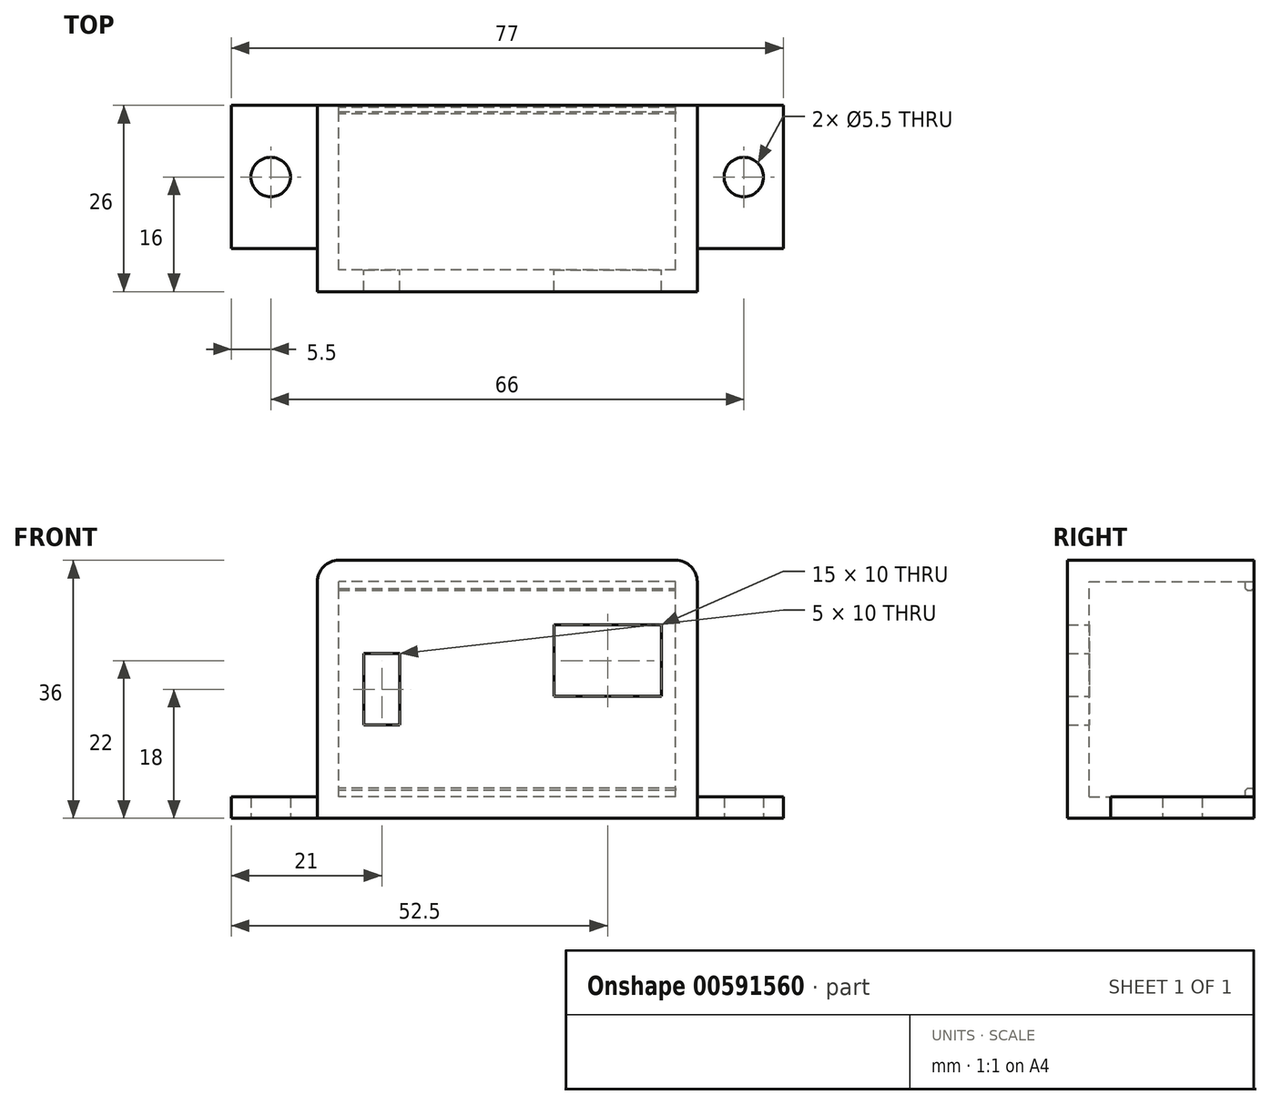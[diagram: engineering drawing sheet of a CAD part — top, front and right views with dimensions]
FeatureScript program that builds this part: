
annotation { "Feature Type Name" : "Feature", "Feature Type Description" : "" }
export const myFeature = defineFeature(function(context is Context, id is Id, definition is map)
    precondition{}
    {
        {
            var Q0;
            Q0=qCreatedBy(makeId("Front.planeOp"),FACE);
            var sketch = newSketch(context, id + "F0", { "sketchPlane" : qUnion([Q0])});
            skLineSegment(sketch, "E0.bottom", {"start": v(26.5, -18) * mm, "end": v(-26.5, -18) * mm});
            skLineSegment(sketch, "E0.top", {"start": v(26.5, 18) * mm, "end": v(-26.5, 18) * mm});
            skLineSegment(sketch, "E0.left", {"start": v(26.5, -18) * mm, "end": v(26.5, 18) * mm});
            skLineSegment(sketch, "E0.right", {"start": v(-26.5, -18) * mm, "end": v(-26.5, 18) * mm});
            skPoint(sketch, "E0.middle", {"position": v(0, 0) * mm});
            skLineSegment(sketch, "E1.bottom", {"start": v(23.5, -15) * mm, "end": v(-23.5, -15) * mm});
            skLineSegment(sketch, "E1.top", {"start": v(23.5, 15) * mm, "end": v(-23.5, 15) * mm});
            skLineSegment(sketch, "E1.left", {"start": v(23.5, -15) * mm, "end": v(23.5, 15) * mm});
            skLineSegment(sketch, "E1.right", {"start": v(-23.5, -15) * mm, "end": v(-23.5, 15) * mm});
            skLineSegment(sketch, "E2.bottom", {"start": v(26.5, -18) * mm, "end": v(38.5, -18) * mm});
            skLineSegment(sketch, "E2.top", {"start": v(26.5, -15) * mm, "end": v(38.5, -15) * mm});
            skLineSegment(sketch, "E2.left", {"start": v(26.5, -18) * mm, "end": v(26.5, -15) * mm});
            skLineSegment(sketch, "E2.right", {"start": v(38.5, -18) * mm, "end": v(38.5, -15) * mm});
            skLineSegment(sketch, "E3.bottom", {"start": v(-26.5, -18) * mm, "end": v(-38.5, -18) * mm});
            skLineSegment(sketch, "E3.top", {"start": v(-26.5, -15) * mm, "end": v(-38.5, -15) * mm});
            skLineSegment(sketch, "E3.left", {"start": v(-26.5, -18) * mm, "end": v(-26.5, -15) * mm});
            skLineSegment(sketch, "E3.right", {"start": v(-38.5, -18) * mm, "end": v(-38.5, -15) * mm});
            skSolve(sketch);
        }
        {
            var Q0;
            Q0=makeQuery(id+"F0.imprint","IMPRINT",FACE,{"disambiguationData":[TD([[makeQuery(id+"F0.imprint","IMPRINT",EDGE,{"derivedFrom":sQuery(id+"F0.wireOp",EDGE,"E0.bottom")}),-1.0]])]});
            extrude(context, id + "F1", {"entities" : qUnion([Q0]), "depth" : 23 * mm, "offsetDistance" : 25 * mm});
        }
        {
            var Q0;
            Q0=makeQuery(id+"F0.imprint","IMPRINT",FACE,{"disambiguationData":[TD([[makeQuery(id+"F0.imprint","IMPRINT",EDGE,{"derivedFrom":sQuery(id+"F0.wireOp",EDGE,"E3.bottom")}),-1.0]])]});
            var Q1;
            Q1=makeQuery(id+"F0.imprint","IMPRINT",FACE,{"disambiguationData":[TD([[makeQuery(id+"F0.imprint","IMPRINT",EDGE,{"derivedFrom":sQuery(id+"F0.wireOp",EDGE,"E2.bottom")}),1.0]])]});
            extrude(context, id + "F2", {"entities" : qUnion([Q0, Q1]), "operationType" : NewBodyOperationType.ADD, "depth" : 20 * mm, "offsetDistance" : 25 * mm});
        }
        {
            var Q0;
            Q0=makeQuery(id+"F1.opExtrude","CAP_FACE",FACE,{"disambiguationData":[OSD([sQuery(id+"F0.wireOp",EDGE,"E0.bottom"),sQuery(id+"F0.wireOp",EDGE,"E0.top"),sQuery(id+"F0.wireOp",EDGE,"E0.left"),sQuery(id+"F0.wireOp",EDGE,"E0.right"),sQuery(id+"F0.wireOp",EDGE,"E1.bottom"),sQuery(id+"F0.wireOp",EDGE,"E1.top"),sQuery(id+"F0.wireOp",EDGE,"E1.left"),sQuery(id+"F0.wireOp",EDGE,"E1.right"),sQuery(id+"F0.wireOp",EDGE,"E2.bottom"),sQuery(id+"F0.wireOp",EDGE,"E2.top"),sQuery(id+"F0.wireOp",EDGE,"E2.right"),sQuery(id+"F0.wireOp",EDGE,"E3.bottom"),sQuery(id+"F0.wireOp",EDGE,"E3.top"),sQuery(id+"F0.wireOp",EDGE,"E3.right")])],"isStart":true});
            var sketch = newSketch(context, id + "F3", { "sketchPlane" : qUnion([Q0])});
            skLineSegment(sketch, "E4.bottom", {"start": v(23.5, -13.8) * mm, "end": v(-23.5, -13.8) * mm});
            skLineSegment(sketch, "E4.top", {"start": v(23.5, 13.8) * mm, "end": v(-23.5, 13.8) * mm});
            skLineSegment(sketch, "E4.left", {"start": v(23.5, -13.8) * mm, "end": v(23.5, 13.8) * mm});
            skLineSegment(sketch, "E4.right", {"start": v(-23.5, -13.8) * mm, "end": v(-23.5, 13.8) * mm});
            skPoint(sketch, "E4.middle", {"position": v(0, 0) * mm});
            skSolve(sketch);
        }
        {
            var Q0;
            {var subQ0=sQuery(id+"F3.wireOp",EDGE,"E4.top");Q0=makeQuery(id+"F3.imprint","IMPRINT",FACE,{"disambiguationData":[TD([[makeQuery(id+"F3.imprint","IMPRINT",EDGE,{"derivedFrom":subQ0}),-1.0]])]});}
            var Q1;
            {var subQ0=sQuery(id+"F3.wireOp",EDGE,"E4.bottom");Q1=makeQuery(id+"F3.imprint","IMPRINT",FACE,{"disambiguationData":[TD([[makeQuery(id+"F3.imprint","IMPRINT",EDGE,{"derivedFrom":subQ0}),1.0]])]});}
            extrude(context, id + "F4", {"entities" : qUnion([Q0, Q1]), "oppositeDirection" : true, "depth" : 1.2 * mm, "offsetDistance" : 25 * mm});
        }
        {
            var Q0;
            Q0=makeQuery(id+"F4.opExtrude","CAP_EDGE",EDGE,{"disambiguationData":[OSD([sQuery(id+"F3.wireOp",EDGE,"E4.bottom")])],"isStart":true});
            var Q1;
            Q1=makeQuery(id+"F4.opExtrude","CAP_EDGE",EDGE,{"disambiguationData":[OSD([sQuery(id+"F3.wireOp",EDGE,"E4.bottom")])],"isStart":false});
            var Q2;
            Q2=makeQuery(id+"F4.opExtrude","CAP_EDGE",EDGE,{"disambiguationData":[OSD([sQuery(id+"F3.wireOp",EDGE,"E4.top")])],"isStart":true});
            var Q3;
            Q3=makeQuery(id+"F4.opExtrude","CAP_EDGE",EDGE,{"disambiguationData":[OSD([sQuery(id+"F3.wireOp",EDGE,"E4.top")])],"isStart":false});
            chamfer(context, id + "F5", {"entities" : qUnion([Q0, Q1, Q2, Q3]), "width" : .3 * mm, "tangentPropagation" : true});
        }
        {
            var Q0;
            Q0=makeQuery(id+"F2.opExtrude","SWEPT_FACE",FACE,{"disambiguationData":[OSD([sQuery(id+"F0.wireOp",EDGE,"E3.top")])]});
            var sketch = newSketch(context, id + "F6", { "sketchPlane" : qUnion([Q0])});
            skPoint(sketch, "E5", {"position": v(-33, -10) * mm});
            skSolve(sketch);
        }
        {
            var Q0;
            Q0=makeQuery(id+"F2.opExtrude","SWEPT_FACE",FACE,{"disambiguationData":[OSD([sQuery(id+"F0.wireOp",EDGE,"E2.top")])]});
            var sketch = newSketch(context, id + "F7", { "sketchPlane" : qUnion([Q0])});
            skPoint(sketch, "E6", {"position": v(33, -10) * mm});
            skSolve(sketch);
        }
        {
            var Q0;
            Q0=sQuery(id+"F6.wireOp",VERTEX,"E5");
            var Q1;
            Q1=sQuery(id+"F7.wireOp",VERTEX,"E6");
            var Q2;
            Q2=makeQuery(id+"F1.opExtrude","SWEPT_BODY",BODY,{"disambiguationData":[OSD([sQuery(id+"F0.wireOp",EDGE,"E0.bottom"),sQuery(id+"F0.wireOp",EDGE,"E0.top"),sQuery(id+"F0.wireOp",EDGE,"E0.left"),sQuery(id+"F0.wireOp",EDGE,"E0.right"),sQuery(id+"F0.wireOp",EDGE,"E1.bottom"),sQuery(id+"F0.wireOp",EDGE,"E1.top"),sQuery(id+"F0.wireOp",EDGE,"E1.left"),sQuery(id+"F0.wireOp",EDGE,"E1.right"),sQuery(id+"F0.wireOp",EDGE,"E2.bottom"),sQuery(id+"F0.wireOp",EDGE,"E2.top"),sQuery(id+"F0.wireOp",EDGE,"E2.right"),sQuery(id+"F0.wireOp",EDGE,"E3.bottom"),sQuery(id+"F0.wireOp",EDGE,"E3.top"),sQuery(id+"F0.wireOp",EDGE,"E3.right")])]});
            hole(context, id + "F8", {"style" : HoleStyle.SIMPLE, "endStyle" : HoleEndStyle.THROUGH, "standardTappedOrClearance" : lookupTablePath({ "standard" : "ISO", "fit" : "Normal", "size" : "M5", "type" : "Clearance" }), "standardBlindInLast" : lookupTablePath({ "fit" : "Standard", "standard" : "ISO", "size" : "M5", "type" : "Clearance" }), "holeDiameter" : 5.5 * mm, "majorDiameter" : 5 * mm, "isTappedThrough" : true, "tappedDepth" : 12 * mm, "tapClearance" : 3, "locations" : qUnion([Q0, Q1]), "scope" : qUnion([Q2])});
        }
        {
            var Q0;
            Q0=makeQuery(id+"F1.opExtrude","CAP_FACE",FACE,{"disambiguationData":[OSD([sQuery(id+"F0.wireOp",EDGE,"E0.bottom"),sQuery(id+"F0.wireOp",EDGE,"E0.top"),sQuery(id+"F0.wireOp",EDGE,"E0.left"),sQuery(id+"F0.wireOp",EDGE,"E0.right"),sQuery(id+"F0.wireOp",EDGE,"E1.bottom"),sQuery(id+"F0.wireOp",EDGE,"E1.top"),sQuery(id+"F0.wireOp",EDGE,"E1.left"),sQuery(id+"F0.wireOp",EDGE,"E1.right"),sQuery(id+"F0.wireOp",EDGE,"E2.left"),sQuery(id+"F0.wireOp",EDGE,"E3.left")])],"isStart":false});
            var sketch = newSketch(context, id + "F9", { "sketchPlane" : qUnion([Q0]), "disableImprinting" : false});
            skPoint(sketch, "E7.middle", {"position": v(-26.5, 18) * mm});
            skLineSegment(sketch, "E8.bottom", {"start": v(-26.5, 18) * mm, "end": v(26.5, 18) * mm});
            skLineSegment(sketch, "E8.top", {"start": v(-26.5, -18) * mm, "end": v(26.5, -18) * mm});
            skLineSegment(sketch, "E8.left", {"start": v(-26.5, 18) * mm, "end": v(-26.5, -18) * mm});
            skLineSegment(sketch, "E8.right", {"start": v(26.5, 18) * mm, "end": v(26.5, -18) * mm});
            skLineSegment(sketch, "E9.bottom", {"start": v(6.5, 9) * mm, "end": v(21.5, 9) * mm});
            skLineSegment(sketch, "E9.top", {"start": v(6.5, -1) * mm, "end": v(21.5, -1) * mm});
            skLineSegment(sketch, "E9.left", {"start": v(6.5, 9) * mm, "end": v(6.5, -1) * mm});
            skLineSegment(sketch, "E9.right", {"start": v(21.5, 9) * mm, "end": v(21.5, -1) * mm});
            skLineSegment(sketch, "E10.bottom", {"start": v(-20, 5) * mm, "end": v(-15, 5) * mm});
            skLineSegment(sketch, "E10.top", {"start": v(-20, -5) * mm, "end": v(-15, -5) * mm});
            skLineSegment(sketch, "E10.left", {"start": v(-20, 5) * mm, "end": v(-20, -5) * mm});
            skLineSegment(sketch, "E10.right", {"start": v(-15, 5) * mm, "end": v(-15, -5) * mm});
            skLineSegment(sketch, "E11", {"start": v(26.5, 0) * mm, "end": v(-26.5, 0) * mm, "construction": true});
            skSolve(sketch);
        }
        {
            var Q0;
            Q0 = qSketchRegion(id + "F9", true);
            extrude(context, id + "F10", {"entities" : qUnion([Q0]), "operationType" : NewBodyOperationType.ADD, "depth" : 3 * mm, "offsetDistance" : 25 * mm});
        }
        {
            var Q0;
            Q0=makeQuery(id+"F2.opExtrude","SWEPT_EDGE",EDGE,{"disambiguationData":[OSD([sQuery(id+"F0.wireOp",EDGE,"E0.right"),sQuery(id+"F0.wireOp",EDGE,"E3.top"),sQuery(id+"F0.wireOp",EDGE,"E3.left")])]});
            var Q1;
            Q1=makeQuery(id+"F10.boolean.opBoolean","MERGE",EDGE,{"derivedFrom":[makeQuery(id+"F1.opExtrude","SWEPT_EDGE",EDGE,{"disambiguationData":[OSD([sQuery(id+"F0.wireOp",EDGE,"E0.top"),sQuery(id+"F0.wireOp",EDGE,"E0.right")])]}),makeQuery(id+"F10.opExtrude","SWEPT_EDGE",EDGE,{"disambiguationData":[OSD([sQuery(id+"F9.wireOp",EDGE,"E8.bottom"),sQuery(id+"F9.wireOp",EDGE,"E8.left")])]})]});
            var Q2;
            Q2=makeQuery(id+"F10.boolean.opBoolean","MERGE",EDGE,{"derivedFrom":[makeQuery(id+"F1.opExtrude","SWEPT_EDGE",EDGE,{"disambiguationData":[OSD([sQuery(id+"F0.wireOp",EDGE,"E0.top"),sQuery(id+"F0.wireOp",EDGE,"E0.left")])]}),makeQuery(id+"F10.opExtrude","SWEPT_EDGE",EDGE,{"disambiguationData":[OSD([sQuery(id+"F9.wireOp",EDGE,"E8.bottom"),sQuery(id+"F9.wireOp",EDGE,"E8.right")])]})]});
            var Q3;
            Q3=makeQuery(id+"F2.opExtrude","SWEPT_EDGE",EDGE,{"disambiguationData":[OSD([sQuery(id+"F0.wireOp",EDGE,"E0.left"),sQuery(id+"F0.wireOp",EDGE,"E2.top"),sQuery(id+"F0.wireOp",EDGE,"E2.left")])]});
            var Q4;
            Q4=makeQuery(id+"F2.opExtrude","CAP_EDGE",EDGE,{"disambiguationData":[OSD([sQuery(id+"F0.wireOp",EDGE,"E2.left")])],"isStart":false});
            var Q5;
            Q5=makeQuery(id+"F2.opExtrude","CAP_EDGE",EDGE,{"disambiguationData":[OSD([sQuery(id+"F0.wireOp",EDGE,"E3.left")])],"isStart":false});
            fillet(context, id + "F11", {"entities" : qUnion([Q0, Q1, Q2, Q3, Q4, Q5]), "radius" : 3 * mm, "tangentPropagation" : true, "allowEdgeOverflow" : false});
        }
    });
